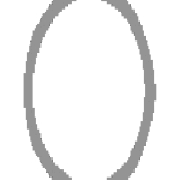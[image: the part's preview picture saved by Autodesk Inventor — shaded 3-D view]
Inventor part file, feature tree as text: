
AUTODESK INVENTOR PART (.ipt)
format: ipt  version: 2021 (Build 250183000, 183)  size: 110,080 bytes
history: native  units: in
note: dims shown in document units (in); Inventor stores cm internally (conversion verified against a paired STEP export)
features: other x4, sketch x3, plane x1
ambient origin geometry x8: Origin, YZ Plane, XZ Plane, XY Plane, X Axis, Y Axis, Z Axis, Center Point
bodies: Solid1 (feature_tree), Body (feature_tree)
feature tree (8):
  other  "Driven Length"
  other  "Frame Generator"
  other  "Start Plane"
  other  "End Plane"
  sketch  "Sketch"  dims[d2=13.2634in d4=-0.0in d5=13.2634in d6=0.12in d7=0.0in d8=90.0deg d9=13.2634in]
  sketch  "Sketch2"  dims[d0=1.0in]
  plane  "Work Plane3"
  sketch  "Sketch3"  dims[d1=0.065in]
